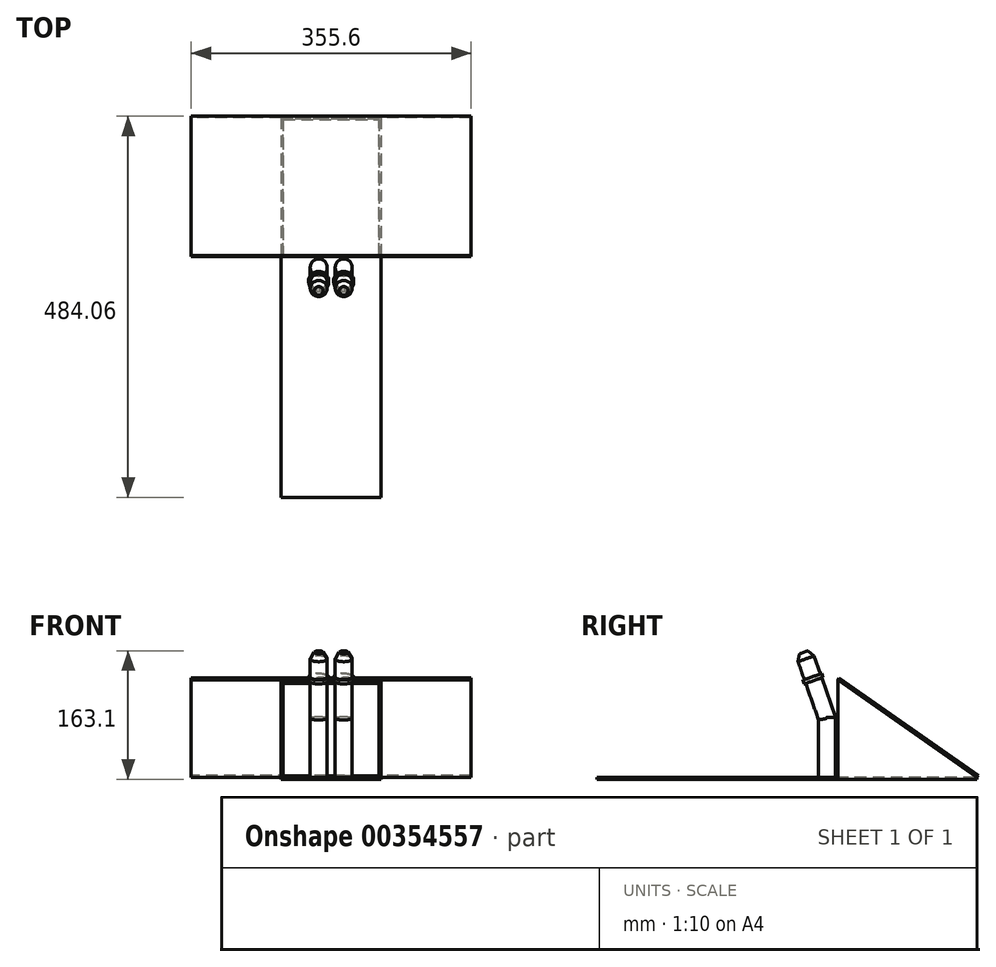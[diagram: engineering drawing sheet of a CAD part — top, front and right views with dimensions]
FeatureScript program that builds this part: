
annotation { "Feature Type Name" : "Feature", "Feature Type Description" : "" }
export const myFeature = defineFeature(function(context is Context, id is Id, definition is map)
    precondition{}
    {
        {
            var Q0;
            Q0=qCreatedBy(makeId("Top.planeOp"),FACE);
            var sketch = newSketch(context, id + "F0", { "sketchPlane" : qUnion([Q0])});
            skLineSegment(sketch, "E0.bottom", {"start": v(63.5, 88.9) * mm, "end": v(-63.5, 88.9) * mm});
            skLineSegment(sketch, "E0.top", {"start": v(63.5, -241.3) * mm, "end": v(-63.5, -241.3) * mm});
            skLineSegment(sketch, "E0.left", {"start": v(63.5, 88.9) * mm, "end": v(63.5, -241.3) * mm});
            skLineSegment(sketch, "E0.right", {"start": v(-63.5, 88.9) * mm, "end": v(-63.5, -241.3) * mm});
            skPoint(sketch, "E1", {"position": v(0, 88.9) * mm});
            skSolve(sketch);
        }
        {
            var Q0;
            Q0=makeQuery(id+"F0.imprint","IMPRINT",FACE,{"disambiguationData":[TD([[makeQuery(id+"F0.imprint","IMPRINT",EDGE,{"derivedFrom":sQuery(id+"F0.wireOp",EDGE,"E0.bottom")}),1.0]])]});
            extrude(context, id + "F1", {"entities" : qUnion([Q0]), "depth" : 2.54 * mm});
        }
        {
            var Q0;
            Q0=makeQuery(id+"F1.opExtrude","CAP_FACE",FACE,{"disambiguationData":[OSD([sQuery(id+"F0.wireOp",EDGE,"E0.bottom"),sQuery(id+"F0.wireOp",EDGE,"E0.top"),sQuery(id+"F0.wireOp",EDGE,"E0.left"),sQuery(id+"F0.wireOp",EDGE,"E0.right")])],"isStart":false});
            var sketch = newSketch(context, id + "F2", { "sketchPlane" : qUnion([Q0])});
            skCircle(sketch, "E2", {"center": v(-15.87, 50.8) * mm, "radius": 10.8 * mm});
            skCircle(sketch, "E3", {"center": v(15.87, 50.8) * mm, "radius": 10.8 * mm});
            skLineSegment(sketch, "E4", {"start": v(-15.87, 50.8) * mm, "end": v(15.87, 50.8) * mm, "construction": true});
            skLineSegment(sketch, "E5", {"start": v(0, 50.8) * mm, "end": v(0, 0) * mm, "construction": true});
            skSolve(sketch);
        }
        {
            var Q0;
            Q0=makeQuery(id+"F2.imprint","IMPRINT",FACE,{"disambiguationData":[TD([[makeQuery(id+"F2.imprint","IMPRINT",EDGE,{"derivedFrom":sQuery(id+"F2.wireOp",EDGE,"E2")}),1.0]])]});
            var Q1;
            Q1=makeQuery(id+"F2.imprint","IMPRINT",FACE,{"disambiguationData":[TD([[makeQuery(id+"F2.imprint","IMPRINT",EDGE,{"derivedFrom":sQuery(id+"F2.wireOp",EDGE,"E3")}),1.0]])]});
            extrude(context, id + "F3", {"entities" : qUnion([Q0, Q1]), "operationType" : NewBodyOperationType.ADD, "depth" : 76.2 * mm});
        }
        {
            var Q0;
            Q0=makeQuery(id+"F1.opExtrude","CAP_EDGE",EDGE,{"disambiguationData":[OSD([sQuery(id+"F0.wireOp",EDGE,"E0.top")])],"isStart":false});
            cPlane(context, id + "F4", {"entities" : qUnion([Q0]), "cplaneType" : CPlaneType.LINE_ANGLE, "offset" : 25.4 * mm, "angle" : 70.5 * degree, "width" : 152.4 * mm, "height" : 152.4 * mm});
        }
        {
            var Q0;
            Q0=qCreatedBy(id+"F4.planeOp",FACE);
            cPlane(context, id + "F5", {"entities" : qUnion([Q0]), "cplaneType" : CPlaneType.OFFSET, "offset" : 49.28 * mm, "width" : 152.4 * mm, "height" : 152.4 * mm});
        }
        {
            var Q0;
            Q0=qCreatedBy(id+"F5.planeOp",FACE);
            var sketch = newSketch(context, id + "F6", { "sketchPlane" : qUnion([Q0])});
            skCircle(sketch, "E6", {"center": v(-15.87, 73.66) * mm, "radius": 10.8 * mm});
            skCircle(sketch, "E7", {"center": v(15.87, 73.66) * mm, "radius": 10.8 * mm});
            skLineSegment(sketch, "E8", {"start": v(-15.87, 73.66) * mm, "end": v(15.87, 73.66) * mm, "construction": true});
            skLineSegment(sketch, "E9", {"start": v(0, 73.66) * mm, "end": v(0, 0) * mm, "construction": true});
            skSolve(sketch);
        }
        {
            var Q0;
            Q0=makeQuery(id+"F6.imprint","IMPRINT",FACE,{"disambiguationData":[TD([[makeQuery(id+"F6.imprint","IMPRINT",EDGE,{"derivedFrom":sQuery(id+"F6.wireOp",EDGE,"E6")}),1.0]])]});
            var Q1;
            Q1=makeQuery(id+"F6.imprint","IMPRINT",FACE,{"disambiguationData":[TD([[makeQuery(id+"F6.imprint","IMPRINT",EDGE,{"derivedFrom":sQuery(id+"F6.wireOp",EDGE,"E7")}),1.0]])]});
            var Q2;
            Q2=makeQuery(id+"F3.opExtrude","CAP_FACE",FACE,{"disambiguationData":[OSD([sQuery(id+"F2.wireOp",EDGE,"E2"),sQuery(id+"F2.wireOp",EDGE,"rLqxtFfq-FP9N-sEGM-Tu7t-yzWMc5ycYLTl")])],"isStart":false});
            extrude(context, id + "F7", {"entities" : qUnion([Q0, Q1]), "oppositeDirection" : true, "endBoundEntityFace" : qUnion([Q2]), "depth" : 81.28 * mm, "hasSecondDirection" : true, "secondDirectionOppositeDirection" : true, "secondDirectionDepth" : 12.7 * mm});
        }
        {
            var Q0;
            Q0=makeQuery(id+"F3.opExtrude","CAP_FACE",FACE,{"disambiguationData":[OSD([sQuery(id+"F2.wireOp",EDGE,"E2"),sQuery(id+"F2.wireOp",EDGE,"rLqxtFfq-FP9N-sEGM-Tu7t-yzWMc5ycYLTl")])],"isStart":false});
            var Q1;
            Q1=makeQuery(id+"F3.opExtrude","CAP_FACE",FACE,{"disambiguationData":[OSD([sQuery(id+"F2.wireOp",EDGE,"E3"),sQuery(id+"F2.wireOp",EDGE,"RpTBqsVt-MdEF-yTbC-rpln-RZPLp5Qrcy98")])],"isStart":false});
            extrude(context, id + "F8", {"entities" : qUnion([Q0, Q1]), "depth" : 70.61 * mm});
        }
        {
            var Q0;
            Q0=makeQuery(id+"F7.opExtrude","SWEPT_BODY",BODY,{"disambiguationData":[OSD([sQuery(id+"F6.wireOp",EDGE,"E6")])]});
            var Q1;
            Q1=makeQuery(id+"F8.opExtrude","SWEPT_BODY",BODY,{"disambiguationData":[OSD([sQuery(id+"F2.wireOp",EDGE,"E2"),sQuery(id+"F2.wireOp",EDGE,"rLqxtFfq-FP9N-sEGM-Tu7t-yzWMc5ycYLTl")])]});
            booleanBodies(context, id + "F9", {"operationType" : BooleanOperationType.INTERSECTION, "tools" : qUnion([Q0, Q1])});
        }
        {
            var Q0;
            Q0=makeQuery(id+"F7.opExtrude","SWEPT_BODY",BODY,{"disambiguationData":[OSD([sQuery(id+"F6.wireOp",EDGE,"E7")])]});
            var Q1;
            Q1=makeQuery(id+"F8.opExtrude","SWEPT_BODY",BODY,{"disambiguationData":[OSD([sQuery(id+"F2.wireOp",EDGE,"E3")])]});
            booleanBodies(context, id + "F10", {"operationType" : BooleanOperationType.INTERSECTION, "tools" : qUnion([Q0, Q1])});
        }
        {
            var Q0;
            Q0=makeQuery(id+"F3.opExtrude","CAP_FACE",FACE,{"disambiguationData":[OSD([sQuery(id+"F2.wireOp",EDGE,"E2")])],"isStart":false});
            var Q1;
            Q1=makeQuery(id+"F9.opBoolean","SPLIT",FACE,{"disambiguationData":[OD(0.0)],"derivedFrom":makeQuery(id+"F7.opExtrude","SWEPT_FACE",FACE,{"disambiguationData":[OSD([sQuery(id+"F6.wireOp",EDGE,"E6")])]})});
            extrude(context, id + "F11", {"entities" : qUnion([Q0]), "operationType" : NewBodyOperationType.ADD, "endBound" : BoundingType.UP_TO_NEXT, "endBoundEntityFace" : qUnion([Q1]), "depth" : 25.4 * mm});
        }
        {
            var Q0;
            Q0=makeQuery(id+"F3.opExtrude","CAP_FACE",FACE,{"disambiguationData":[OSD([sQuery(id+"F2.wireOp",EDGE,"E3")])],"isStart":false});
            extrude(context, id + "F12", {"entities" : qUnion([Q0]), "operationType" : NewBodyOperationType.ADD, "endBound" : BoundingType.UP_TO_NEXT, "depth" : 25.4 * mm});
        }
        {
            var Q0;
            Q0=makeQuery(id+"F6.imprint","IMPRINT",FACE,{"disambiguationData":[TD([[makeQuery(id+"F6.imprint","IMPRINT",EDGE,{"derivedFrom":sQuery(id+"F6.wireOp",EDGE,"E6")}),1.0]])]});
            var Q1;
            Q1=makeQuery(id+"F6.imprint","IMPRINT",FACE,{"disambiguationData":[TD([[makeQuery(id+"F6.imprint","IMPRINT",EDGE,{"derivedFrom":sQuery(id+"F6.wireOp",EDGE,"E7")}),1.0]])]});
            extrude(context, id + "F13", {"entities" : qUnion([Q0, Q1]), "operationType" : NewBodyOperationType.ADD, "depth" : 12.7 * mm, "hasSecondDirection" : true, "secondDirectionBound" : SecondDirectionBoundingType.UP_TO_NEXT, "secondDirectionOppositeDirection" : true, "secondDirectionDepth" : 25.4 * mm});
        }
        {
            var Q0;
            Q0=makeQuery(id+"F13.opExtrude","CAP_EDGE",EDGE,{"disambiguationData":[OSD([sQuery(id+"F6.wireOp",EDGE,"E6")])],"isStart":false});
            var Q1;
            Q1=makeQuery(id+"F13.opExtrude","CAP_EDGE",EDGE,{"disambiguationData":[OSD([sQuery(id+"F6.wireOp",EDGE,"E7")])],"isStart":false});
            chamfer(context, id + "F14", {"entities" : qUnion([Q0, Q1]), "chamferType" : ChamferType.OFFSET_ANGLE, "width" : 5.08 * mm, "oppositeDirection" : false, "angle" : 60 * degree, "tangentPropagation" : true});
        }
        {
            var Q0;
            Q0=qCreatedBy(makeId("Top.planeOp"),FACE);
            var sketch = newSketch(context, id + "F15", { "sketchPlane" : qUnion([Q0])});
            skLineSegment(sketch, "E10.bottom", {"start": v(-63.5, 88.9) * mm, "end": v(63.5, 88.9) * mm});
            skLineSegment(sketch, "E10.top", {"start": v(-63.5, 241.3) * mm, "end": v(63.5, 241.3) * mm});
            skLineSegment(sketch, "E10.left", {"start": v(-63.5, 88.9) * mm, "end": v(-63.5, 241.3) * mm});
            skLineSegment(sketch, "E10.right", {"start": v(63.5, 88.9) * mm, "end": v(63.5, 241.3) * mm});
            skSolve(sketch);
        }
        {
            var Q0;
            Q0=makeQuery(id+"F15.imprint","IMPRINT",FACE,{"disambiguationData":[TD([[makeQuery(id+"F15.imprint","IMPRINT",EDGE,{"derivedFrom":sQuery(id+"F15.wireOp",EDGE,"E10.bottom")}),1.0]])]});
            extrude(context, id + "F16", {"entities" : qUnion([Q0]), "operationType" : NewBodyOperationType.ADD, "depth" : 2.54 * mm});
        }
        {
            var Q0;
            Q0=makeQuery(id+"F13.opExtrude","CAP_FACE",FACE,{"disambiguationData":[OSD([sQuery(id+"F6.wireOp",EDGE,"E6")])],"isStart":false});
            var sketch = newSketch(context, id + "F17", { "sketchPlane" : qUnion([Q0])});
            skCircle(sketch, "E11", {"center": v(-15.87, 73.66) * mm, "radius": 12.7 * mm});
            skCircle(sketch, "E12", {"center": v(15.87, 73.66) * mm, "radius": 12.7 * mm});
            skSolve(sketch);
        }
        {
            var Q0;
            Q0=makeQuery(id+"F17.imprint","IMPRINT",FACE,{"disambiguationData":[TD([[makeQuery(id+"F17.imprint","IMPRINT",EDGE,{"derivedFrom":sQuery(id+"F17.wireOp",EDGE,"E11")}),1.0]])]});
            var Q1;
            {var subQ0=sQuery(id+"F6.wireOp",EDGE,"E6");Q1=makeQuery(id+"F17.imprint","IMPRINT",FACE,{"disambiguationData":[TD([[makeQuery(id+"F17.imprint","IMPRINT",EDGE,{"derivedFrom":makeQuery(id+"F14.opChamfer","BLEND_EDGE",EDGE,{"blendedFrom":[makeQuery(id+"F13.opExtrude","CAP_EDGE",EDGE,{"disambiguationData":[OSD([subQ0])],"isStart":false}),makeQuery(id+"F13.opExtrude","CAP_FACE",FACE,{"disambiguationData":[OSD([subQ0])],"isStart":false})],"blendedInto":[makeQuery(id+"F13.opExtrude","CAP_FACE",FACE,{"disambiguationData":[OSD([subQ0])],"isStart":false})]})}),1.0]])]});}
            var Q2;
            Q2=makeQuery(id+"F17.imprint","IMPRINT",FACE,{"disambiguationData":[TD([[makeQuery(id+"F17.imprint","IMPRINT",EDGE,{"derivedFrom":sQuery(id+"F17.wireOp",EDGE,"E12")}),1.0]])]});
            extrude(context, id + "F18", {"entities" : qUnion([Q0, Q1, Q2]), "operationType" : NewBodyOperationType.ADD, "oppositeDirection" : true, "depth" : 38.1 * mm, "hasSecondDirection" : true, "secondDirectionOppositeDirection" : true, "secondDirectionDepth" : 33.02 * mm});
        }
        {
            var Q0;
            Q0=makeQuery(id+"F16.opExtrude","CAP_EDGE",EDGE,{"disambiguationData":[OSD([sQuery(id+"F15.wireOp",EDGE,"E10.top")])],"isStart":false});
            cPlane(context, id + "F19", {"entities" : qUnion([Q0]), "cplaneType" : CPlaneType.LINE_ANGLE, "offset" : 25.4 * mm, "angle" : 55 * degree, "width" : 152.4 * mm, "height" : 152.4 * mm});
        }
        {
            var Q0;
            Q0=qCreatedBy(id+"F19.planeOp",FACE);
            var sketch = newSketch(context, id + "F20", { "sketchPlane" : qUnion([Q0])});
            skLineSegment(sketch, "E13.bottom", {"start": v(177.8, 196.2) * mm, "end": v(-177.8, 196.2) * mm});
            skLineSegment(sketch, "E13.top", {"start": v(177.8, -19.7) * mm, "end": v(-177.8, -19.7) * mm});
            skLineSegment(sketch, "E13.left", {"start": v(177.8, 196.2) * mm, "end": v(177.8, -19.7) * mm});
            skLineSegment(sketch, "E13.right", {"start": v(-177.8, 196.2) * mm, "end": v(-177.8, -19.7) * mm});
            skPoint(sketch, "E14", {"position": v(0, 196.2) * mm});
            skSolve(sketch);
        }
        {
            var Q0;
            Q0=makeQuery(id+"F20.imprint","IMPRINT",FACE,{"disambiguationData":[TD([[makeQuery(id+"F20.imprint","IMPRINT",EDGE,{"derivedFrom":sQuery(id+"F20.wireOp",EDGE,"E13.bottom")}),1.0]])]});
            extrude(context, id + "F21", {"entities" : qUnion([Q0]), "depth" : 2.54 * mm});
        }
        {
            var Q0;
            Q0=makeQuery(id+"F16.boolean.opBoolean","MERGE",FACE,{"derivedFrom":[makeQuery(id+"F1.opExtrude","CAP_FACE",FACE,{"disambiguationData":[OSD([sQuery(id+"F0.wireOp",EDGE,"E0.bottom"),sQuery(id+"F0.wireOp",EDGE,"E0.top"),sQuery(id+"F0.wireOp",EDGE,"E0.left"),sQuery(id+"F0.wireOp",EDGE,"E0.right")])],"isStart":false}),makeQuery(id+"F16.opExtrude","CAP_FACE",FACE,{"disambiguationData":[OSD([sQuery(id+"F15.wireOp",EDGE,"E10.bottom"),sQuery(id+"F15.wireOp",EDGE,"E10.top"),sQuery(id+"F15.wireOp",EDGE,"E10.left"),sQuery(id+"F15.wireOp",EDGE,"E10.right")])],"isStart":false})]});
            var sketch = newSketch(context, id + "F22", { "sketchPlane" : qUnion([Q0])});
            skLineSegment(sketch, "E15.bottom", {"start": v(-63.5, 64.45) * mm, "end": v(63.5, 64.45) * mm});
            skLineSegment(sketch, "E15.top", {"start": v(-63.5, 241.3) * mm, "end": v(63.5, 241.3) * mm});
            skLineSegment(sketch, "E15.left", {"start": v(-63.5, 64.45) * mm, "end": v(-63.5, 241.3) * mm});
            skLineSegment(sketch, "E15.right", {"start": v(63.5, 64.45) * mm, "end": v(63.5, 241.3) * mm});
            skSolve(sketch);
        }
        {
            var Q0;
            Q0=makeQuery(id+"F22.imprint","IMPRINT",FACE,{"disambiguationData":[TD([[makeQuery(id+"F22.imprint","IMPRINT",EDGE,{"derivedFrom":sQuery(id+"F22.wireOp",EDGE,"E15.bottom")}),1.0]])]});
            var Q1;
            Q1=makeQuery(id+"F21.opExtrude","CAP_FACE",FACE,{"disambiguationData":[OSD([sQuery(id+"F20.wireOp",EDGE,"E13.bottom"),sQuery(id+"F20.wireOp",EDGE,"E13.top"),sQuery(id+"F20.wireOp",EDGE,"E13.left"),sQuery(id+"F20.wireOp",EDGE,"E13.right")])],"isStart":true});
            extrude(context, id + "F23", {"entities" : qUnion([Q0]), "operationType" : NewBodyOperationType.ADD, "endBound" : BoundingType.UP_TO_SURFACE, "endBoundEntityFace" : qUnion([Q1]), "depth" : 25.4 * mm});
        }
        {
            var Q0;
            Q0=makeQuery(id+"F23.opExtrude","SWEPT_FACE",FACE,{"disambiguationData":[OSD([sQuery(id+"F22.wireOp",EDGE,"E15.bottom")])]});
            shell(context, id + "F24", {"entities" : qUnion([Q0]), "thickness" : 2.54 * mm});
        }
    });
